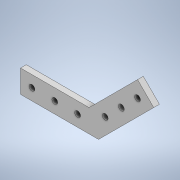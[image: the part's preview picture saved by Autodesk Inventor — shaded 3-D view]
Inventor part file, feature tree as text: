
AUTODESK INVENTOR PART (.ipt)
format: ipt  version: 2020 (Build 240168000, 168)  size: 120,832 bytes
history: native  units: in
note: dims shown in document units (in); Inventor stores cm internally (conversion verified against a paired STEP export)
features: extrude x1, sketch x1
ambient origin geometry x8: Origin, YZ Plane, XZ Plane, XY Plane, X Axis, Y Axis, Z Axis, Center Point
bodies: Solid1 (feature_tree)
feature tree (2):
  extrude  "Extrusion1"  Depth=0.25in
  sketch  "Sketch1"  dims[d0=1.0in d1=3.0in d2=3.0in d3=135.0deg d4=1.0in d5=0.256in d6=0.5in d7=1.1811in d9=1.0in d10=0.3937in d12=1.0in d14=0.5in d15=0.256in d16=0.5in d17=0.5in d18=0.3937in d20=1.0in d21=1.1811in d23=1.0in d25=0.25in d26=0.0in]
